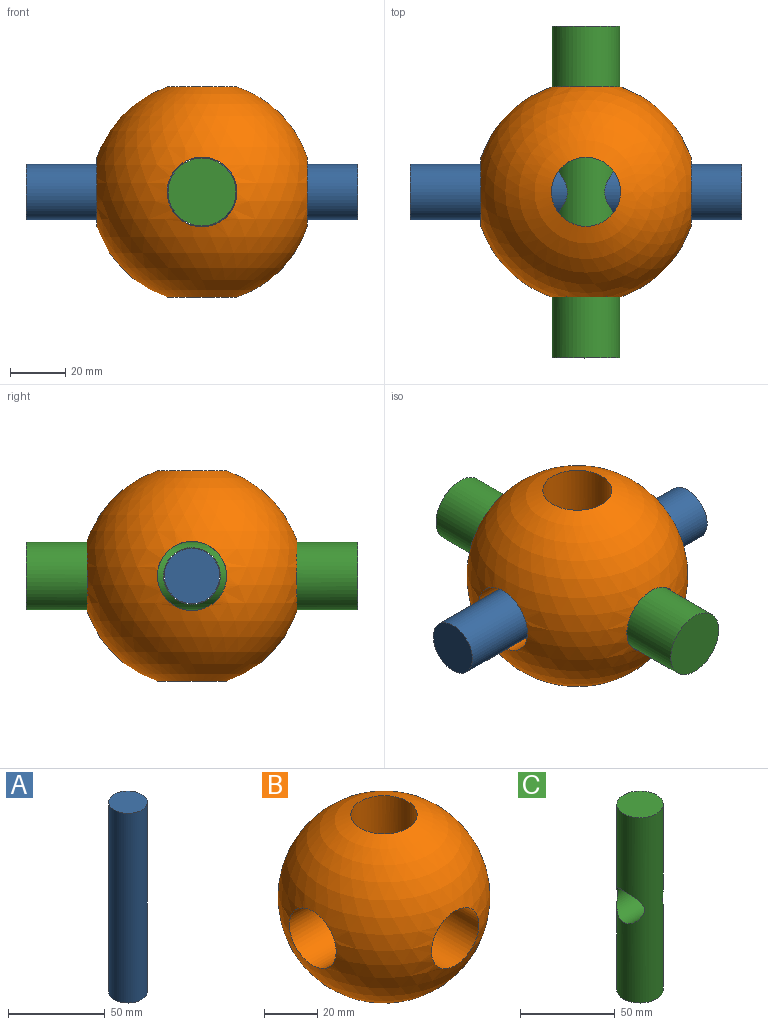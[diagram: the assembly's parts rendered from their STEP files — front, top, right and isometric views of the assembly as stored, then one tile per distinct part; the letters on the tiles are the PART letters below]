
ASSEMBLY  parts=3 mates=4
PART A: 3 faces, bbox 20x20x120 mm
  f0: cylinder r=10mm len=120mm, axis (0,0,-1), area 7539.8mm2, adj f1,f2
  f1: plane 20x20mm, normal (0,0,1), area 314.2mm2, adj f0
  f2: plane 20x20mm, normal (0,0,-1), area 314.2mm2, adj f0
PART B: 7 faces, bbox 80x80x76 mm
  f0: cylinder r=12.62mm len=29.2mm, axis (0,-1,0), area 2119.4mm2, adj f1,f2,f3,f5,f6
  f1: cylinder r=12.5mm len=29.07mm, axis (-1,0,0), area 2095.1mm2, adj f0,f2,f4,f5,f6
  f2: sphere r=40mm, area 17065.5mm2, adj f0,f1,f3,f4,f5,f6
  f3: cylinder r=12.5mm len=29.07mm, axis (-1,0,0), area 2095.1mm2, adj f0,f2,f4,f5,f6
  f4: cylinder r=12.62mm len=29.2mm, axis (0,-1,0), area 2119.4mm2, adj f1,f2,f3,f5,f6
  f5: cylinder r=12.5mm len=29.07mm, axis (0,0,1), area 2095.1mm2, adj f0,f1,f2,f3,f4
  f6: cylinder r=12.5mm len=29.07mm, axis (0,0,1), area 2095.1mm2, adj f0,f1,f2,f3,f4
PART C: 4 faces, bbox 24.5x24.5x120 mm
  f0: cylinder r=12.25mm len=120mm, axis (0,0,-1), area 8493mm2, adj f1,f2,f3
  f1: plane 24.5x24.5mm, normal (0,0,1), area 471.4mm2, adj f0
  f2: plane 24.5x24.5mm, normal (0,0,-1), area 471.4mm2, adj f0
  f3: cylinder r=10.25mm len=24.5mm, axis (1,0,0), area 1247.2mm2, adj f0
PLACE A rot(axis=(0.71,0,0.71),180deg) t=(-157.04,70.66,3.32)mm
PLACE B t=(-93.41,70.66,3.32)mm
PLACE C rot(axis=(-1,0,0),90deg) t=(-93.41,70.66,3.32)mm
MATE cylindrical C.f0 <-> B.f0  axis (0,-1,0) through (-93.41,130.66,3.32)mm
MATE slider A.f0 <-> C.f3  axis (-1,0,0) through (-157.04,70.66,3.32)mm
MATE slider C.f3 <-> B.f1  axis (1,0,0) through (-80.99,70.66,3.32)mm
MATE slider C.f0 <-> B.f0  axis (0,-1,0) through (-93.41,70.66,3.32)mm
